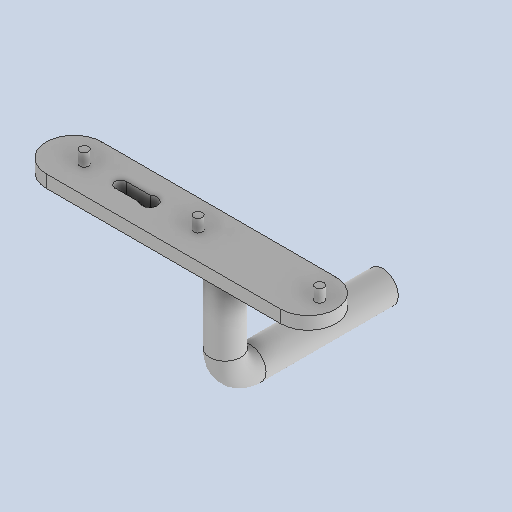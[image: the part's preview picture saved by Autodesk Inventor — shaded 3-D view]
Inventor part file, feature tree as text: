
AUTODESK INVENTOR PART (.ipt)
format: ipt  version: 2025.1 (Build 291241000, 241)  size: 131,584 bytes
history: native  units: mm
features: other x4, sketch x4, plane x1
ambient origin geometry x8: Origin, YZ Plane, XZ Plane, XY Plane, X Axis, Y Axis, Z Axis, Center Point
bodies: Body1 (feature_tree)
feature tree (9):
  other  "garnitur_lang.ipt"
  other  "Solid2::garnitur_lang.ipt"
  other  "TaggingFeature1"
  sketch  "Sketch1"  dims[d0=10.0mm]
  sketch  "Sketch2"
  sketch  "Sketch5"
  sketch  "Sketch6"
  plane  "Work Plane1"
  other  "Work Point1"
